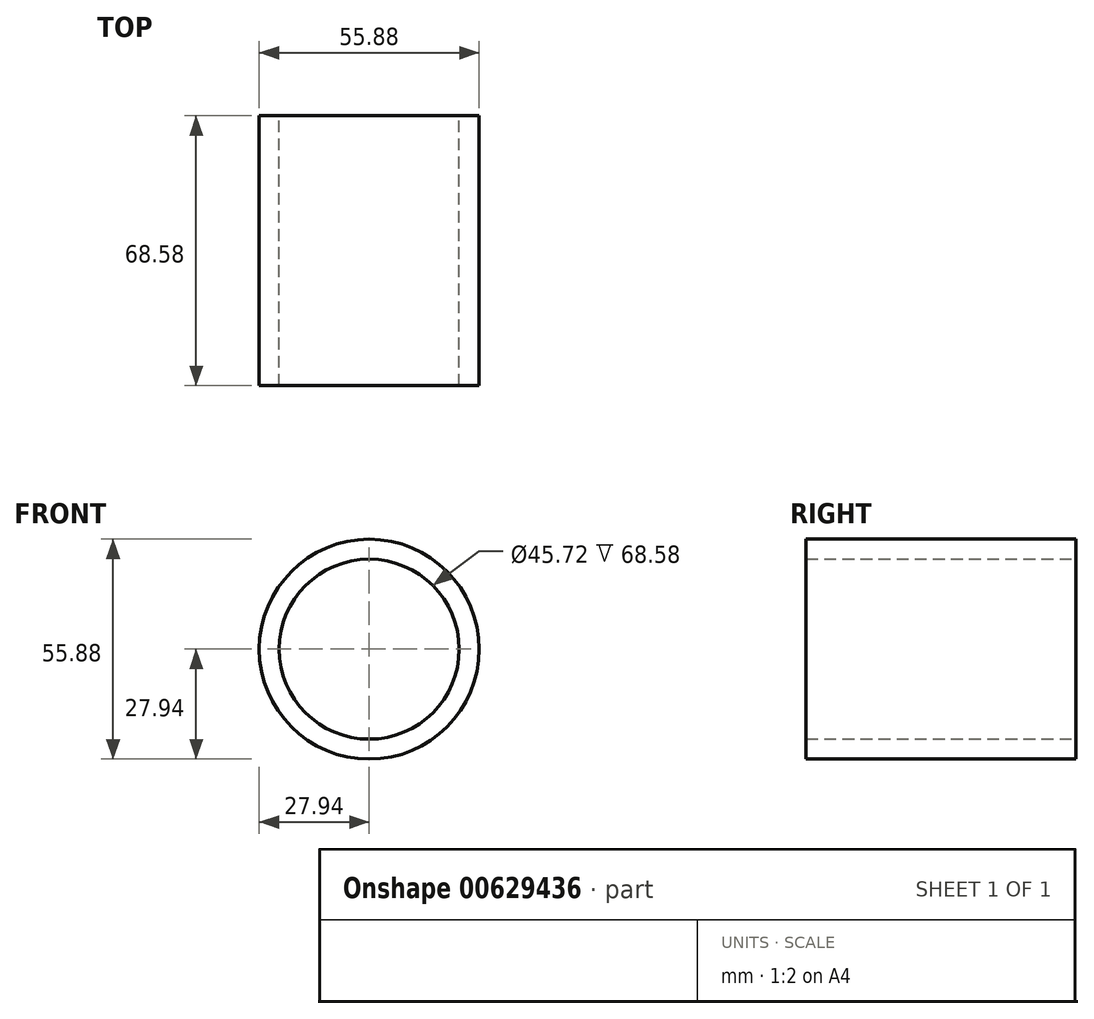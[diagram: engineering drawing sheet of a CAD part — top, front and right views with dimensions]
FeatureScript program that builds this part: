
annotation { "Feature Type Name" : "Feature", "Feature Type Description" : "" }
export const myFeature = defineFeature(function(context is Context, id is Id, definition is map)
    precondition{}
    {
        {
            var Q0;
            Q0=qCreatedBy(makeId("Front.planeOp"),FACE);
            var sketch = newSketch(context, id + "F0", { "sketchPlane" : qUnion([Q0])});
            skCircle(sketch, "E0", {"center": v(0, 0) * mm, "radius": 27.94 * mm});
            skCircle(sketch, "E1.0", {"center": v(0, 0) * mm, "radius": 22.86 * mm});
            skSolve(sketch);
        }
        {
            var Q0;
            Q0 = qSketchRegion(id + "F0", true);
            extrude(context, id + "F1", {"entities" : qUnion([Q0]), "depth" : 68.58 * mm, "offsetDistance" : 25.4 * mm});
        }
    });
